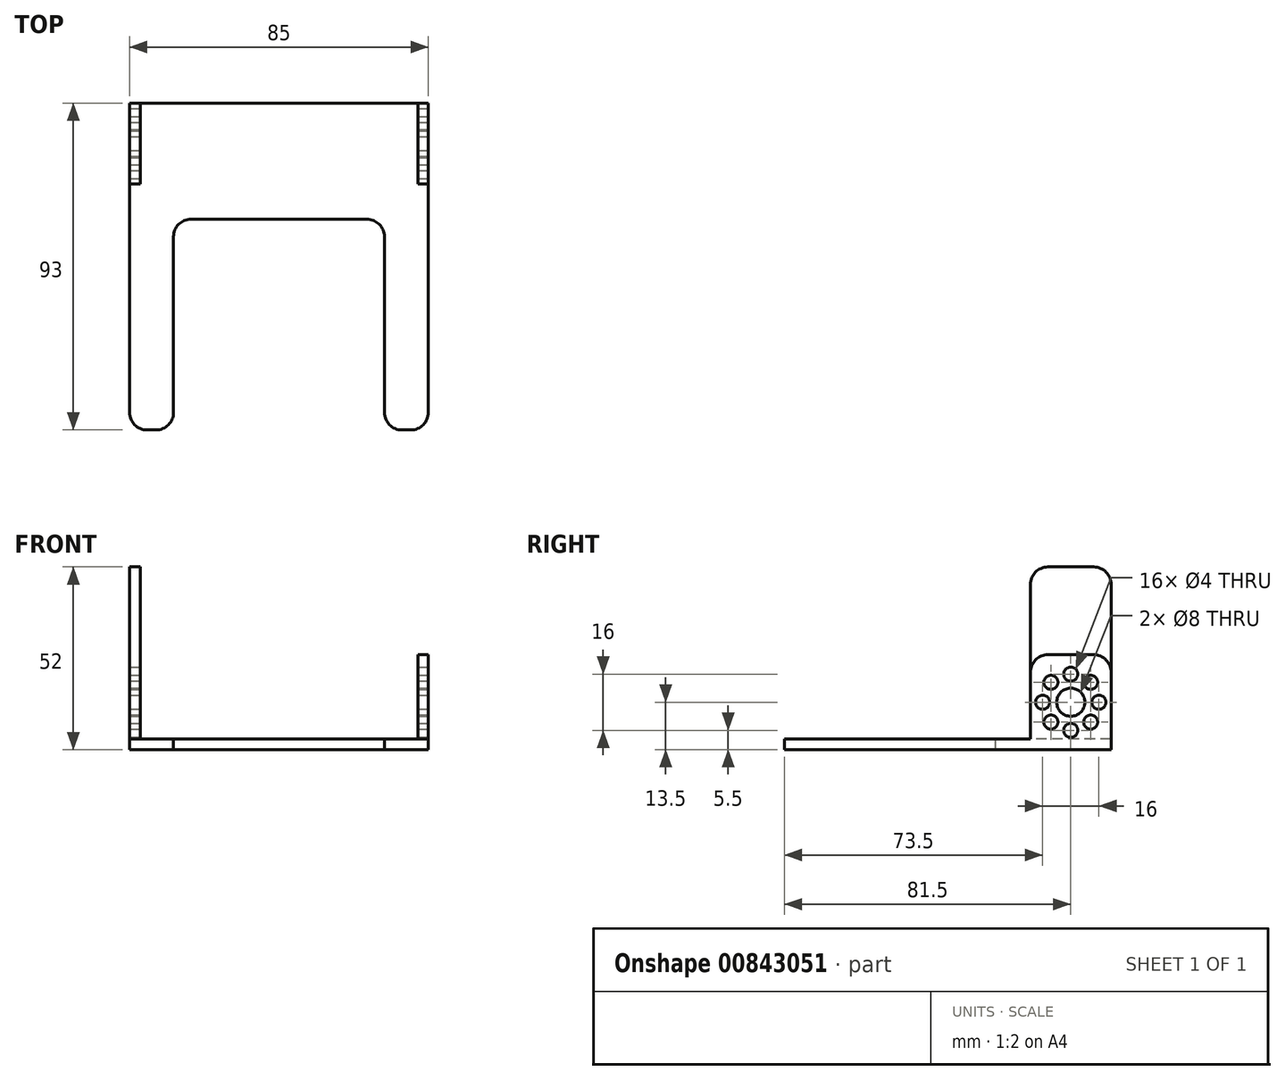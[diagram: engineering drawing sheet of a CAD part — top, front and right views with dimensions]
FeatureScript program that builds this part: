
annotation { "Feature Type Name" : "Feature", "Feature Type Description" : "" }
export const myFeature = defineFeature(function(context is Context, id is Id, definition is map)
    precondition{}
    {
        {
            var Q0;
            Q0=qCreatedBy(makeId("Top.planeOp"),FACE);
            var sketch = newSketch(context, id + "F0", { "sketchPlane" : qUnion([Q0])});
            skLineSegment(sketch, "E0.bottom", {"start": v(0, 0) * mm, "end": v(85, 0) * mm});
            skLineSegment(sketch, "E0.top", {"start": v(0, 23) * mm, "end": v(85, 23) * mm});
            skLineSegment(sketch, "E0.left", {"start": v(0, 0) * mm, "end": v(0, 23) * mm});
            skLineSegment(sketch, "E0.right", {"start": v(85, 0) * mm, "end": v(85, 23) * mm});
            skLineSegment(sketch, "E1.top", {"start": v(17.5, -10) * mm, "end": v(67.5, -10) * mm});
            skLineSegment(sketch, "E1.left", {"start": v(0, 0) * mm, "end": v(0, -10) * mm});
            skLineSegment(sketch, "E1.right", {"start": v(85, 0) * mm, "end": v(85, -10) * mm});
            skLineSegment(sketch, "E2.top", {"start": v(5, -70) * mm, "end": v(7.5, -70) * mm});
            skLineSegment(sketch, "E2.left", {"start": v(0, -10) * mm, "end": v(0, -65) * mm});
            skLineSegment(sketch, "E2.right", {"start": v(12.5, -15) * mm, "end": v(12.5, -65) * mm});
            skLineSegment(sketch, "E3.top", {"start": v(80, -70) * mm, "end": v(77.5, -70) * mm});
            skLineSegment(sketch, "E3.left", {"start": v(85, -10) * mm, "end": v(85, -65) * mm});
            skLineSegment(sketch, "E3.right", {"start": v(72.5, -15) * mm, "end": v(72.5, -65) * mm});
            skPoint(sketch, "E4.visualSharp", {"position": v(12.5, -70) * mm});
            skArc(sketch, "E4.filletArc", {"start": v(7.5, -70) * mm, "mid": v(11.04, -68.54) * mm, "end": v(12.5, -65) * mm});
            skPoint(sketch, "E5.visualSharp", {"position": v(0, -70) * mm});
            skArc(sketch, "E5.filletArc", {"start": v(0, -65) * mm, "mid": v(1.46, -68.54) * mm, "end": v(5, -70) * mm});
            skPoint(sketch, "E6.visualSharp", {"position": v(72.5, -70) * mm});
            skArc(sketch, "E6.filletArc", {"start": v(72.5, -65) * mm, "mid": v(73.96, -68.54) * mm, "end": v(77.5, -70) * mm});
            skPoint(sketch, "E7.visualSharp", {"position": v(85, -70) * mm});
            skArc(sketch, "E7.filletArc", {"start": v(80, -70) * mm, "mid": v(83.54, -68.54) * mm, "end": v(85, -65) * mm});
            skPoint(sketch, "E8.visualSharp", {"position": v(12.5, -10) * mm});
            skArc(sketch, "E8.filletArc", {"start": v(17.5, -10) * mm, "mid": v(13.96, -11.46) * mm, "end": v(12.5, -15) * mm});
            skPoint(sketch, "E9.visualSharp", {"position": v(72.5, -10) * mm});
            skArc(sketch, "E9.filletArc", {"start": v(72.5, -15) * mm, "mid": v(71.04, -11.46) * mm, "end": v(67.5, -10) * mm});
            skSolve(sketch);
        }
        {
            var Q0;
            Q0=qSketchRegion(id+"F0",true);
            extrude(context, id + "F1", {"entities" : qUnion([Q0]), "depth" : 3 * mm, "offsetDistance" : 25 * mm});
        }
        {
            var Q0;
            Q0=makeQuery(id+"F1.opExtrude","CAP_FACE",FACE,{"disambiguationData":[OSD([sQuery(id+"F0.wireOp",EDGE,"E0.bottom"),sQuery(id+"F0.wireOp",EDGE,"E0.top"),sQuery(id+"F0.wireOp",EDGE,"E0.left"),sQuery(id+"F0.wireOp",EDGE,"E0.right")])],"isStart":false});
            var sketch = newSketch(context, id + "F2", { "sketchPlane" : qUnion([Q0])});
            skLineSegment(sketch, "E10.bottom", {"start": v(0, 23) * mm, "end": v(3, 23) * mm});
            skLineSegment(sketch, "E10.top", {"start": v(0, 0) * mm, "end": v(3, 0) * mm});
            skLineSegment(sketch, "E10.left", {"start": v(0, 23) * mm, "end": v(0, 0) * mm});
            skLineSegment(sketch, "E10.right", {"start": v(3, 23) * mm, "end": v(3, 0) * mm});
            skLineSegment(sketch, "E11.bottom", {"start": v(85, 23) * mm, "end": v(82, 23) * mm});
            skLineSegment(sketch, "E11.top", {"start": v(85, 0) * mm, "end": v(82, 0) * mm});
            skLineSegment(sketch, "E11.left", {"start": v(85, 23) * mm, "end": v(85, 0) * mm});
            skLineSegment(sketch, "E11.right", {"start": v(82, 23) * mm, "end": v(82, 0) * mm});
            skSolve(sketch);
        }
        {
            var Q0;
            Q0=qSketchRegion(id+"F2",true);
            extrude(context, id + "F3", {"entities" : qUnion([Q0]), "operationType" : NewBodyOperationType.ADD, "depth" : 24 * mm, "offsetDistance" : 25 * mm});
        }
        {
            var Q0;
            Q0=makeQuery(id+"F3.opExtrude","CAP_FACE",FACE,{"disambiguationData":[OSD([sQuery(id+"F2.wireOp",EDGE,"E10.bottom"),sQuery(id+"F2.wireOp",EDGE,"E10.top"),sQuery(id+"F2.wireOp",EDGE,"E10.left"),sQuery(id+"F2.wireOp",EDGE,"E10.right")])],"isStart":false});
            var sketch = newSketch(context, id + "F4", { "sketchPlane" : qUnion([Q0])});
            skLineSegment(sketch, "E12.bottom", {"start": v(0, 23) * mm, "end": v(3, 23) * mm});
            skLineSegment(sketch, "E12.top", {"start": v(0, 0) * mm, "end": v(3, 0) * mm});
            skLineSegment(sketch, "E12.left", {"start": v(0, 23) * mm, "end": v(0, 0) * mm});
            skLineSegment(sketch, "E12.right", {"start": v(3, 23) * mm, "end": v(3, 0) * mm});
            skSolve(sketch);
        }
        {
            var Q0;
            Q0=qSketchRegion(id+"F4",true);
            extrude(context, id + "F5", {"entities" : qUnion([Q0]), "operationType" : NewBodyOperationType.ADD, "depth" : 25 * mm, "offsetDistance" : 25 * mm});
        }
        {
            var Q0;
            Q0=makeQuery(id+"F3.boolean.opBoolean","MERGE",FACE,{"derivedFrom":[makeQuery(id+"F1.opExtrude","SWEPT_FACE",FACE,{"disambiguationData":[OSD([sQuery(id+"F0.wireOp",EDGE,"E0.right"),sQuery(id+"F0.wireOp",EDGE,"E1.right"),sQuery(id+"F0.wireOp",EDGE,"E3.left")])]}),makeQuery(id+"F3.opExtrude","SWEPT_FACE",FACE,{"disambiguationData":[OSD([sQuery(id+"F2.wireOp",EDGE,"E11.left")])]})]});
            var sketch = newSketch(context, id + "F6", { "sketchPlane" : qUnion([Q0])});
            skLineSegment(sketch, "E13", {"start": v(23, 0) * mm, "end": v(23, 27) * mm});
            skCircle(sketch, "E14", {"center": v(11.5, 13.5) * mm, "radius": 4 * mm});
            skPoint(sketch, "E15.orphan", {"position": v(0, 27) * mm});
            skLineSegment(sketch, "E16", {"start": v(11.5, 13.5) * mm, "end": v(0, 13.5) * mm, "construction": true});
            skLineSegment(sketch, "E17", {"start": v(11.5, 13.5) * mm, "end": v(23, 13.5) * mm, "construction": true});
            skCircle(sketch, "E18", {"center": v(19.5, 13.5) * mm, "radius": 2 * mm});
            skCircle(sketch, "E19.1.0", {"center": v(17.16, 19.16) * mm, "radius": 2 * mm});
            skCircle(sketch, "E19.2.0", {"center": v(11.5, 21.5) * mm, "radius": 2 * mm});
            skCircle(sketch, "E19.3.0", {"center": v(5.84, 19.16) * mm, "radius": 2 * mm});
            skCircle(sketch, "E19.4.0", {"center": v(3.5, 13.5) * mm, "radius": 2 * mm});
            skCircle(sketch, "E19.5.0", {"center": v(5.84, 7.84) * mm, "radius": 2 * mm});
            skCircle(sketch, "E19.6.0", {"center": v(11.5, 5.5) * mm, "radius": 2 * mm});
            skCircle(sketch, "E19.7.0", {"center": v(17.16, 7.84) * mm, "radius": 2 * mm});
            skSolve(sketch);
        }
        {
            var Q0;
            Q0=makeQuery(id+"F6.imprint","IMPRINT",FACE,{"disambiguationData":[TD([[makeQuery(id+"F6.imprint","IMPRINT",EDGE,{"derivedFrom":sQuery(id+"F6.wireOp",EDGE,"E14")}),1.0]])]});
            var Q1;
            Q1=makeQuery(id+"F6.imprint","IMPRINT",FACE,{"disambiguationData":[TD([[makeQuery(id+"F6.imprint","IMPRINT",EDGE,{"derivedFrom":sQuery(id+"F6.wireOp",EDGE,"E19.3.0")}),1.0]])]});
            var Q2;
            Q2=makeQuery(id+"F6.imprint","IMPRINT",FACE,{"disambiguationData":[TD([[makeQuery(id+"F6.imprint","IMPRINT",EDGE,{"derivedFrom":sQuery(id+"F6.wireOp",EDGE,"E19.2.0")}),1.0]])]});
            var Q3;
            Q3=makeQuery(id+"F6.imprint","IMPRINT",FACE,{"disambiguationData":[TD([[makeQuery(id+"F6.imprint","IMPRINT",EDGE,{"derivedFrom":sQuery(id+"F6.wireOp",EDGE,"E19.1.0")}),1.0]])]});
            var Q4;
            Q4=makeQuery(id+"F6.imprint","IMPRINT",FACE,{"disambiguationData":[TD([[makeQuery(id+"F6.imprint","IMPRINT",EDGE,{"derivedFrom":sQuery(id+"F6.wireOp",EDGE,"E18")}),1.0]])]});
            var Q5;
            Q5=makeQuery(id+"F6.imprint","IMPRINT",FACE,{"disambiguationData":[TD([[makeQuery(id+"F6.imprint","IMPRINT",EDGE,{"derivedFrom":sQuery(id+"F6.wireOp",EDGE,"E19.7.0")}),1.0]])]});
            var Q6;
            Q6=makeQuery(id+"F6.imprint","IMPRINT",FACE,{"disambiguationData":[TD([[makeQuery(id+"F6.imprint","IMPRINT",EDGE,{"derivedFrom":sQuery(id+"F6.wireOp",EDGE,"E19.6.0")}),1.0]])]});
            var Q7;
            Q7=makeQuery(id+"F6.imprint","IMPRINT",FACE,{"disambiguationData":[TD([[makeQuery(id+"F6.imprint","IMPRINT",EDGE,{"derivedFrom":sQuery(id+"F6.wireOp",EDGE,"E19.5.0")}),1.0]])]});
            var Q8;
            Q8=makeQuery(id+"F6.imprint","IMPRINT",FACE,{"disambiguationData":[TD([[makeQuery(id+"F6.imprint","IMPRINT",EDGE,{"derivedFrom":sQuery(id+"F6.wireOp",EDGE,"E19.4.0")}),1.0]])]});
            extrude(context, id + "F7", {"entities" : qUnion([Q0, Q1, Q2, Q3, Q4, Q5, Q6, Q7, Q8]), "operationType" : NewBodyOperationType.REMOVE, "oppositeDirection" : true, "depth" : 250 * mm, "offsetDistance" : 25 * mm});
        }
        {
            var Q0;
            Q0=makeQuery(id+"F5.opExtrude","CAP_EDGE",EDGE,{"disambiguationData":[OSD([sQuery(id+"F4.wireOp",EDGE,"E12.bottom")])],"isStart":false});
            var Q1;
            Q1=makeQuery(id+"F5.opExtrude","CAP_EDGE",EDGE,{"disambiguationData":[OSD([sQuery(id+"F4.wireOp",EDGE,"E12.top")])],"isStart":false});
            var Q2;
            Q2=makeQuery(id+"F3.opExtrude","CAP_EDGE",EDGE,{"disambiguationData":[OSD([sQuery(id+"F2.wireOp",EDGE,"E11.bottom")])],"isStart":false});
            var Q3;
            Q3=makeQuery(id+"F3.opExtrude","CAP_EDGE",EDGE,{"disambiguationData":[OSD([sQuery(id+"F2.wireOp",EDGE,"E11.top")])],"isStart":false});
            fillet(context, id + "F8", {"entities" : qUnion([Q0, Q1, Q2, Q3]), "radius" : 5 * mm, "tangentPropagation" : true, "allowEdgeOverflow" : false});
        }
    });
